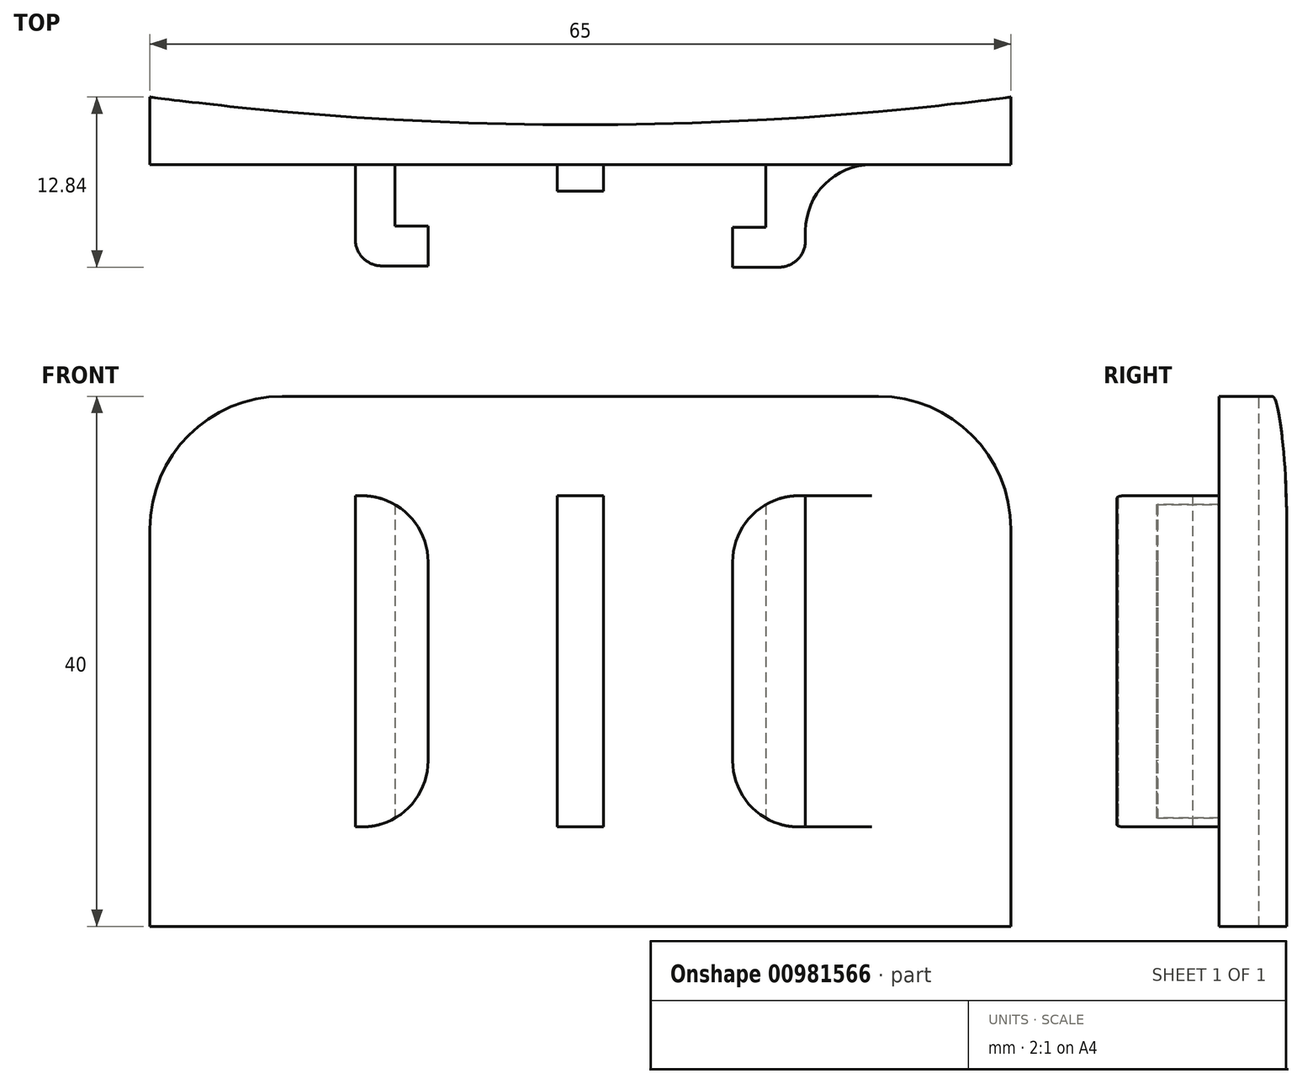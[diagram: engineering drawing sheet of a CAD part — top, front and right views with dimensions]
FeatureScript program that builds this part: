
annotation { "Feature Type Name" : "Feature", "Feature Type Description" : "" }
export const myFeature = defineFeature(function(context is Context, id is Id, definition is map)
    precondition{}
    {
        {
            var Q0;
            Q0=qCreatedBy(makeId("Front.planeOp"),FACE);
            var sketch = newSketch(context, id + "F0", { "sketchPlane" : qUnion([Q0])});
            skLineSegment(sketch, "E0.bottom", {"start": v(32.5, -20) * mm, "end": v(-32.5, -20) * mm});
            skLineSegment(sketch, "E0.top", {"start": v(32.5, 20) * mm, "end": v(-32.5, 20) * mm});
            skLineSegment(sketch, "E0.left", {"start": v(32.5, -20) * mm, "end": v(32.5, 20) * mm});
            skLineSegment(sketch, "E0.right", {"start": v(-32.5, -20) * mm, "end": v(-32.5, 20) * mm});
            skSolve(sketch);
        }
        {
            var Q0;
            Q0=makeQuery(id+"F0.imprint","IMPRINT",FACE,{"disambiguationData":[TD([[makeQuery(id+"F0.imprint","IMPRINT",EDGE,{"derivedFrom":sQuery(id+"F0.wireOp",EDGE,"E0.bottom")}),-1.0]])]});
            extrude(context, id + "F1", {"entities" : qUnion([Q0]), "depth" : 3 * mm, "offsetDistance" : 25 * mm});
        }
        {
            var Q0;
            Q0=makeQuery(id+"F1.opExtrude","SWEPT_FACE",FACE,{"disambiguationData":[OSD([sQuery(id+"F0.wireOp",EDGE,"E0.top")])]});
            var sketch = newSketch(context, id + "F2", { "sketchPlane" : qUnion([Q0])});
            skLineSegment(sketch, "E1", {"start": v(0, 0) * mm, "end": v(-32.5, 0) * mm, "construction": true});
            skArc(sketch, "E2", {"start": v(-32.5, 2.1) * mm, "mid": v(0, 0) * mm, "end": v(32.5, 2.1) * mm});
            skLineSegment(sketch, "E3", {"start": v(-32.5, 0) * mm, "end": v(-32.5, 2.1) * mm});
            skLineSegment(sketch, "E4", {"start": v(32.5, 0) * mm, "end": v(32.5, 2.1) * mm});
            skLineSegment(sketch, "E5", {"start": v(-32.5, 0) * mm, "end": v(32.5, 0) * mm});
            skSolve(sketch);
        }
        {
            var Q0;
            Q0 = qSketchRegion(id + "F2", true);
            var Q1;
            Q1=makeQuery(id+"F1.opExtrude","SWEPT_FACE",FACE,{"disambiguationData":[OSD([sQuery(id+"F0.wireOp",EDGE,"E0.bottom")])]});
            extrude(context, id + "F3", {"entities" : qUnion([Q0]), "operationType" : NewBodyOperationType.ADD, "endBound" : BoundingType.UP_TO_SURFACE, "oppositeDirection" : true, "depth" : 25 * mm, "endBoundEntityFace" : qUnion([Q1]), "offsetDistance" : 25 * mm});
        }
        {
            var Q0;
            {var subQ0=sQuery(id+"F2.wireOp",EDGE,"E5");var subQ1=sQuery(id+"F2.wireOp",EDGE,"E2");Q0=makeQuery(id+"F3.boolean.opBoolean","MERGE",FACE,{"derivedFrom":[makeQuery(id+"F1.opExtrude","SWEPT_FACE",FACE,{"disambiguationData":[OSD([sQuery(id+"F0.wireOp",EDGE,"E0.bottom")])]}),makeQuery(id+"F3.opExtrude","CAP_FACE",FACE,{"disambiguationData":[OSD([subQ1,sQuery(id+"F2.wireOp",EDGE,"E3"),subQ0])],"isStart":false}),makeQuery(id+"F3.opExtrude","CAP_FACE",FACE,{"disambiguationData":[OSD([subQ1,sQuery(id+"F2.wireOp",EDGE,"E4"),subQ0])],"isStart":false})]});}
            var sketch = newSketch(context, id + "F4", { "sketchPlane" : qUnion([Q0])});
            skLineSegment(sketch, "E6", {"start": v(-17, 3) * mm, "end": v(-17, 10.64) * mm});
            skLineSegment(sketch, "E7", {"start": v(-17, 10.64) * mm, "end": v(-11.5, 10.64) * mm});
            skLineSegment(sketch, "E8", {"start": v(-11.5, 10.64) * mm, "end": v(-11.5, 7.64) * mm});
            skLineSegment(sketch, "E9", {"start": v(-11.5, 7.64) * mm, "end": v(-14, 7.64) * mm});
            skLineSegment(sketch, "E10", {"start": v(-14, 7.64) * mm, "end": v(-14, 3) * mm});
            skLineSegment(sketch, "E11", {"start": v(-14, 3) * mm, "end": v(-17, 3) * mm});
            skLineSegment(sketch, "E12", {"start": v(17, 3) * mm, "end": v(17, 10.74) * mm});
            skLineSegment(sketch, "E13", {"start": v(14, 7.74) * mm, "end": v(14, 3) * mm});
            skLineSegment(sketch, "E14", {"start": v(14, 3) * mm, "end": v(17, 3) * mm});
            skLineSegment(sketch, "E15", {"start": v(14, 7.74) * mm, "end": v(11.5, 7.74) * mm});
            skLineSegment(sketch, "E16", {"start": v(11.5, 10.74) * mm, "end": v(17, 10.74) * mm});
            skLineSegment(sketch, "E17", {"start": v(11.5, 10.74) * mm, "end": v(11.5, 7.74) * mm});
            skLineSegment(sketch, "E18.bottom", {"start": v(1.75, 3) * mm, "end": v(-1.75, 3) * mm});
            skLineSegment(sketch, "E18.top", {"start": v(1.75, 5) * mm, "end": v(-1.75, 5) * mm});
            skLineSegment(sketch, "E18.left", {"start": v(1.75, 3) * mm, "end": v(1.75, 5) * mm});
            skLineSegment(sketch, "E18.right", {"start": v(-1.75, 3) * mm, "end": v(-1.75, 5) * mm});
            skSolve(sketch);
        }
        {
            var Q0;
            Q0 = qSketchRegion(id + "F4", true);
            var Q1;
            {var subQ0=sQuery(id+"F2.wireOp",EDGE,"E5");var subQ1=sQuery(id+"F2.wireOp",EDGE,"E2");Q1=makeQuery(id+"F3.boolean.opBoolean","MERGE",FACE,{"derivedFrom":[makeQuery(id+"F1.opExtrude","SWEPT_FACE",FACE,{"disambiguationData":[OSD([sQuery(id+"F0.wireOp",EDGE,"E0.top")])]}),makeQuery(id+"F3.opExtrude","CAP_FACE",FACE,{"disambiguationData":[OSD([subQ1,sQuery(id+"F2.wireOp",EDGE,"E3"),subQ0])],"isStart":true}),makeQuery(id+"F3.opExtrude","CAP_FACE",FACE,{"disambiguationData":[OSD([subQ1,sQuery(id+"F2.wireOp",EDGE,"E4"),subQ0])],"isStart":true})]});}
            extrude(context, id + "F5", {"entities" : qUnion([Q0]), "operationType" : NewBodyOperationType.ADD, "endBound" : BoundingType.UP_TO_SURFACE, "oppositeDirection" : true, "depth" : 25 * mm, "endBoundEntityFace" : qUnion([Q1]), "offsetDistance" : 25 * mm});
        }
        {
            var Q0;
            Q0=makeQuery(id+"F3.boolean.opBoolean","MERGE",FACE,{"derivedFrom":[makeQuery(id+"F1.opExtrude","SWEPT_FACE",FACE,{"disambiguationData":[OSD([sQuery(id+"F0.wireOp",EDGE,"E0.left")])]}),makeQuery(id+"F3.opExtrude","SWEPT_FACE",FACE,{"disambiguationData":[OSD([sQuery(id+"F2.wireOp",EDGE,"E4")])]})]});
            var sketch = newSketch(context, id + "F6", { "sketchPlane" : qUnion([Q0])});
            skLineSegment(sketch, "E19.bottom", {"start": v(-3, -20) * mm, "end": v(-13.02, -20) * mm});
            skLineSegment(sketch, "E19.top", {"start": v(-3, -12.5) * mm, "end": v(-13.02, -12.5) * mm});
            skLineSegment(sketch, "E19.left", {"start": v(-3, -20) * mm, "end": v(-3, -12.5) * mm});
            skLineSegment(sketch, "E19.right", {"start": v(-13.02, -20) * mm, "end": v(-13.02, -12.5) * mm});
            skLineSegment(sketch, "E20.bottom", {"start": v(-3, 20) * mm, "end": v(-16.62, 20) * mm});
            skLineSegment(sketch, "E20.top", {"start": v(-3, 12.5) * mm, "end": v(-16.62, 12.5) * mm});
            skLineSegment(sketch, "E20.left", {"start": v(-3, 20) * mm, "end": v(-3, 12.5) * mm});
            skLineSegment(sketch, "E20.right", {"start": v(-16.62, 20) * mm, "end": v(-16.62, 12.5) * mm});
            skSolve(sketch);
        }
        {
            var Q0;
            Q0=makeQuery(id+"F6.imprint","IMPRINT",FACE,{"disambiguationData":[TD([[makeQuery(id+"F6.imprint","IMPRINT",EDGE,{"derivedFrom":sQuery(id+"F6.wireOp",EDGE,"E19.bottom")}),-1.0]])]});
            var Q1;
            Q1=makeQuery(id+"F6.imprint","IMPRINT",FACE,{"disambiguationData":[TD([[makeQuery(id+"F6.imprint","IMPRINT",EDGE,{"derivedFrom":sQuery(id+"F6.wireOp",EDGE,"E20.bottom")}),1.0]])]});
            var Q2;
            Q2=makeQuery(id+"F3.boolean.opBoolean","MERGE",FACE,{"derivedFrom":[makeQuery(id+"F1.opExtrude","SWEPT_FACE",FACE,{"disambiguationData":[OSD([sQuery(id+"F0.wireOp",EDGE,"E0.right")])]}),makeQuery(id+"F3.opExtrude","SWEPT_FACE",FACE,{"disambiguationData":[OSD([sQuery(id+"F2.wireOp",EDGE,"E3")])]})]});
            extrude(context, id + "F7", {"entities" : qUnion([Q0, Q1]), "operationType" : NewBodyOperationType.REMOVE, "endBound" : BoundingType.UP_TO_SURFACE, "oppositeDirection" : true, "depth" : 25 * mm, "endBoundEntityFace" : qUnion([Q2]), "offsetDistance" : 25 * mm});
        }
        {
            var Q0;
            Q0=makeQuery(id+"F5.opExtrude","SWEPT_EDGE",EDGE,{"disambiguationData":[OSD([sQuery(id+"F0.wireOp",EDGE,"E0.bottom"),sQuery(id+"F4.wireOp",EDGE,"E12"),sQuery(id+"F4.wireOp",EDGE,"E14")])]});
            var Q1;
            Q1=makeQuery(id+"F5.opExtrude","SWEPT_EDGE",EDGE,{"disambiguationData":[OSD([sQuery(id+"F0.wireOp",EDGE,"E0.bottom"),sQuery(id+"F4.wireOp",EDGE,"E6"),sQuery(id+"F4.wireOp",EDGE,"E11")])]});
            fillet(context, id + "F8", {"entities" : qUnion([Q0, Q1]), "radius" : 5 * mm, "tangentPropagation" : true, "allowEdgeOverflow" : false});
        }
        {
            var Q0;
            Q0=makeQuery(id+"F7.boolean.opBoolean","INTERSECT",EDGE,{"derivedFrom":[makeQuery(id+"F5.opExtrude","SWEPT_FACE",FACE,{"disambiguationData":[OSD([sQuery(id+"F4.wireOp",EDGE,"E17")])]}),makeQuery(id+"F7.opExtrude","SWEPT_FACE",FACE,{"disambiguationData":[OSD([sQuery(id+"F6.wireOp",EDGE,"E20.top")])]})]});
            var Q1;
            Q1=makeQuery(id+"F7.boolean.opBoolean","INTERSECT",EDGE,{"derivedFrom":[makeQuery(id+"F5.opExtrude","SWEPT_FACE",FACE,{"disambiguationData":[OSD([sQuery(id+"F4.wireOp",EDGE,"E8")])]}),makeQuery(id+"F7.opExtrude","SWEPT_FACE",FACE,{"disambiguationData":[OSD([sQuery(id+"F6.wireOp",EDGE,"E20.top")])]})]});
            var Q2;
            Q2=makeQuery(id+"F7.boolean.opBoolean","INTERSECT",EDGE,{"derivedFrom":[makeQuery(id+"F5.opExtrude","SWEPT_FACE",FACE,{"disambiguationData":[OSD([sQuery(id+"F4.wireOp",EDGE,"E17")])]}),makeQuery(id+"F7.opExtrude","SWEPT_FACE",FACE,{"disambiguationData":[OSD([sQuery(id+"F6.wireOp",EDGE,"E19.top")])]})]});
            var Q3;
            Q3=makeQuery(id+"F7.boolean.opBoolean","INTERSECT",EDGE,{"derivedFrom":[makeQuery(id+"F5.opExtrude","SWEPT_FACE",FACE,{"disambiguationData":[OSD([sQuery(id+"F4.wireOp",EDGE,"E8")])]}),makeQuery(id+"F7.opExtrude","SWEPT_FACE",FACE,{"disambiguationData":[OSD([sQuery(id+"F6.wireOp",EDGE,"E19.top")])]})]});
            fillet(context, id + "F9", {"entities" : qUnion([Q0, Q1, Q2, Q3]), "radius" : 5 * mm, "tangentPropagation" : true, "allowEdgeOverflow" : false});
        }
        {
            var Q0;
            Q0=makeQuery(id+"F5.opExtrude","SWEPT_EDGE",EDGE,{"disambiguationData":[OSD([sQuery(id+"F4.wireOp",EDGE,"E12"),sQuery(id+"F4.wireOp",EDGE,"E16")])]});
            var Q1;
            Q1=makeQuery(id+"F5.opExtrude","SWEPT_EDGE",EDGE,{"disambiguationData":[OSD([sQuery(id+"F4.wireOp",EDGE,"E6"),sQuery(id+"F4.wireOp",EDGE,"E7")])]});
            fillet(context, id + "F10", {"entities" : qUnion([Q0, Q1]), "radius" : 2 * mm, "tangentPropagation" : true, "allowEdgeOverflow" : false});
        }
        {
            var Q0;
            Q0=makeQuery(id+"F3.boolean.opBoolean","MERGE",EDGE,{"derivedFrom":[makeQuery(id+"F1.opExtrude","SWEPT_EDGE",EDGE,{"disambiguationData":[OSD([sQuery(id+"F0.wireOp",EDGE,"E0.top"),sQuery(id+"F0.wireOp",EDGE,"E0.left")])]}),makeQuery(id+"F3.opExtrude","CAP_EDGE",EDGE,{"disambiguationData":[OSD([sQuery(id+"F2.wireOp",EDGE,"E4")])],"isStart":true})]});
            var Q1;
            Q1=makeQuery(id+"F3.boolean.opBoolean","MERGE",EDGE,{"derivedFrom":[makeQuery(id+"F1.opExtrude","SWEPT_EDGE",EDGE,{"disambiguationData":[OSD([sQuery(id+"F0.wireOp",EDGE,"E0.top"),sQuery(id+"F0.wireOp",EDGE,"E0.right")])]}),makeQuery(id+"F3.opExtrude","CAP_EDGE",EDGE,{"disambiguationData":[OSD([sQuery(id+"F2.wireOp",EDGE,"E3")])],"isStart":true})]});
            fillet(context, id + "F11", {"entities" : qUnion([Q0, Q1]), "radius" : 10 * mm, "tangentPropagation" : true, "allowEdgeOverflow" : false});
        }
    });
